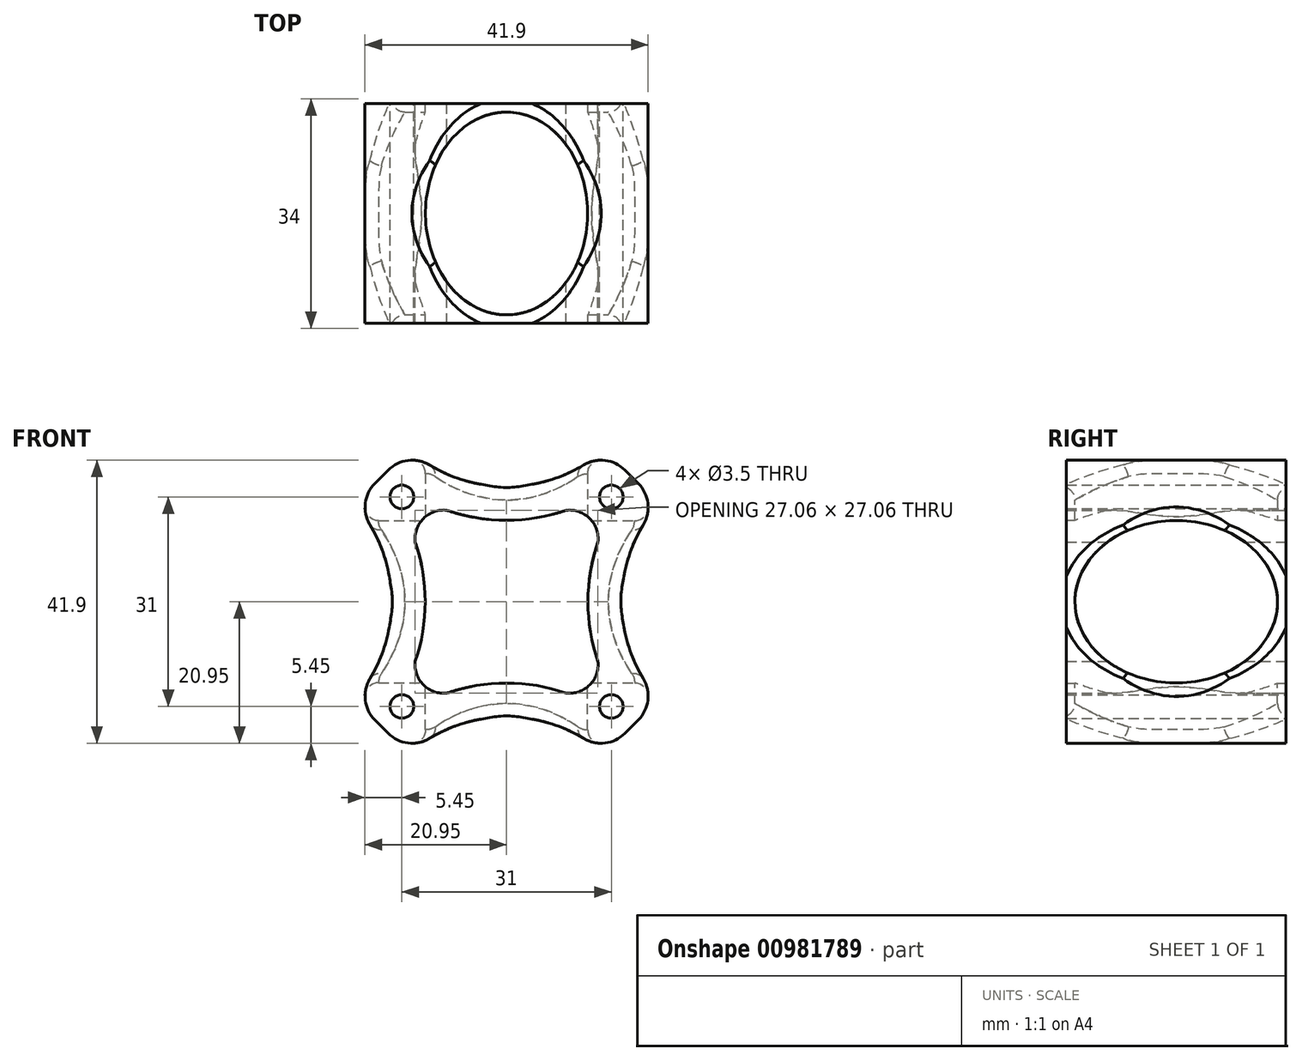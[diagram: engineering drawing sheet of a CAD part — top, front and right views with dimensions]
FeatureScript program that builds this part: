
annotation { "Feature Type Name" : "Feature", "Feature Type Description" : "" }
export const myFeature = defineFeature(function(context is Context, id is Id, definition is map)
    precondition{}
    {
        {
            var Q0;
            Q0=qCreatedBy(makeId("Front.planeOp"),FACE);
            var sketch = newSketch(context, id + "F0", { "sketchPlane" : qUnion([Q0])});
            skLineSegment(sketch, "E0.bottom", {"start": v(-15.5, 15.5) * mm, "end": v(15.5, 15.5) * mm, "construction": true});
            skLineSegment(sketch, "E0.top", {"start": v(-15.5, -15.5) * mm, "end": v(15.5, -15.5) * mm, "construction": true});
            skLineSegment(sketch, "E0.left", {"start": v(-15.5, 15.5) * mm, "end": v(-15.5, -15.5) * mm, "construction": true});
            skLineSegment(sketch, "E0.right", {"start": v(15.5, 15.5) * mm, "end": v(15.5, -15.5) * mm, "construction": true});
            skPoint(sketch, "E0.middle", {"position": v(0, 0) * mm});
            skCircle(sketch, "E1", {"center": v(-15.5, 15.5) * mm, "radius": 2.75 * mm, "construction": true});
            skCircle(sketch, "E2", {"center": v(15.5, 15.5) * mm, "radius": 2.75 * mm, "construction": true});
            skCircle(sketch, "E3", {"center": v(-15.5, -15.5) * mm, "radius": 2.75 * mm, "construction": true});
            skCircle(sketch, "E4", {"center": v(15.5, -15.5) * mm, "radius": 2.75 * mm, "construction": true});
            skCircle(sketch, "E5", {"center": v(0, 0) * mm, "radius": 6.6 * mm});
            skLineSegment(sketch, "E6.bottom", {"start": v(14.5, 22.5) * mm, "end": v(-14.5, 22.5) * mm});
            skLineSegment(sketch, "E6.top", {"start": v(14.5, -22.5) * mm, "end": v(-14.5, -22.5) * mm});
            skLineSegment(sketch, "E6.left", {"start": v(22.5, 14.5) * mm, "end": v(22.5, 0) * mm});
            skLineSegment(sketch, "E6.right", {"start": v(-22.5, 14.5) * mm, "end": v(-22.5, 0) * mm});
            skPoint(sketch, "E7.visualSharp", {"position": v(-22.5, 22.5) * mm});
            skPoint(sketch, "E8.visualSharp", {"position": v(22.5, 22.5) * mm});
            skPoint(sketch, "E9.visualSharp", {"position": v(22.5, -22.5) * mm});
            skPoint(sketch, "E10.visualSharp", {"position": v(-22.5, -22.5) * mm});
            skLineSegment(sketch, "E11", {"start": v(-22.5, 0) * mm, "end": v(-22.5, -14.5) * mm});
            skLineSegment(sketch, "E12", {"start": v(22.5, 0) * mm, "end": v(22.5, -14.5) * mm});
            skArc(sketch, "E13", {"start": v(-22.5, -14.5) * mm, "mid": v(-17.05, 0) * mm, "end": v(-22.5, 14.5) * mm});
            skArc(sketch, "E14", {"start": v(-14.5, 22.5) * mm, "mid": v(0, 17.05) * mm, "end": v(14.5, 22.5) * mm});
            skArc(sketch, "E15", {"start": v(22.5, 14.5) * mm, "mid": v(17.05, 0) * mm, "end": v(22.5, -14.5) * mm});
            skArc(sketch, "E16", {"start": v(14.5, -22.5) * mm, "mid": v(0, -17.05) * mm, "end": v(-14.5, -22.5) * mm});
            skArc(sketch, "E17", {"start": v(-8.83, 13.53) * mm, "mid": v(0, 12.05) * mm, "end": v(8.83, 13.53) * mm});
            skArc(sketch, "E18", {"start": v(-8.83, 13.53) * mm, "mid": v(-12.3, 12.3) * mm, "end": v(-13.53, 8.83) * mm});
            skArc(sketch, "E19.1.0", {"start": v(-13.53, -8.83) * mm, "mid": v(-12.3, -12.3) * mm, "end": v(-8.83, -13.53) * mm});
            skArc(sketch, "E19.2.0", {"start": v(8.83, -13.53) * mm, "mid": v(12.3, -12.3) * mm, "end": v(13.53, -8.83) * mm});
            skArc(sketch, "E19.3.0", {"start": v(13.53, 8.83) * mm, "mid": v(12.3, 12.3) * mm, "end": v(8.83, 13.53) * mm});
            skArc(sketch, "E20", {"start": v(13.53, 8.83) * mm, "mid": v(12.05, 0) * mm, "end": v(13.53, -8.83) * mm});
            skArc(sketch, "E21", {"start": v(8.83, -13.53) * mm, "mid": v(0, -12.05) * mm, "end": v(-8.83, -13.53) * mm});
            skArc(sketch, "E22", {"start": v(-13.53, -8.83) * mm, "mid": v(-12.05, 0) * mm, "end": v(-13.53, 8.83) * mm});
            skLineSegment(sketch, "E23", {"start": v(-22.5, 14.5) * mm, "end": v(-14.5, 22.5) * mm});
            skLineSegment(sketch, "E24", {"start": v(14.5, 22.5) * mm, "end": v(22.5, 14.5) * mm});
            skLineSegment(sketch, "E25", {"start": v(22.5, -14.5) * mm, "end": v(14.5, -22.5) * mm});
            skLineSegment(sketch, "E26", {"start": v(-14.5, -22.5) * mm, "end": v(-22.5, -14.5) * mm});
            skSolve(sketch);
        }
        {
            var Q0;
            Q0=makeQuery(id+"F0.imprint","IMPRINT",FACE,{"disambiguationData":[TD([[makeQuery(id+"F0.imprint","IMPRINT",EDGE,{"derivedFrom":sQuery(id+"F0.wireOp",EDGE,"E13")}),-1.0]])]});
            extrude(context, id + "F1", {"entities" : qUnion([Q0]), "depth" : 32.5 * mm, "offsetDistance" : 25 * mm});
        }
        {
            var Q0;
            Q0=sQuery(id+"F0.wireOp",VERTEX,"E0.bottom.end");
            var Q1;
            Q1=sQuery(id+"F0.wireOp",VERTEX,"E0.bottom.start");
            var Q2;
            Q2=sQuery(id+"F0.wireOp",VERTEX,"E0.top.start");
            var Q3;
            Q3=sQuery(id+"F0.wireOp",VERTEX,"E0.top.end");
            var Q4;
            Q4=makeQuery(id+"F1.opExtrude","SWEPT_BODY",BODY,{"disambiguationData":[OSD([sQuery(id+"F0.wireOp",EDGE,"E7.filletArc"),sQuery(id+"F0.wireOp",EDGE,"E8.filletArc"),sQuery(id+"F0.wireOp",EDGE,"E9.filletArc"),sQuery(id+"F0.wireOp",EDGE,"E10.filletArc"),sQuery(id+"F0.wireOp",EDGE,"E13"),sQuery(id+"F0.wireOp",EDGE,"E14"),sQuery(id+"F0.wireOp",EDGE,"E15"),sQuery(id+"F0.wireOp",EDGE,"E16"),sQuery(id+"F0.wireOp",EDGE,"E17"),sQuery(id+"F0.wireOp",EDGE,"E18"),sQuery(id+"F0.wireOp",EDGE,"E19.1.0"),sQuery(id+"F0.wireOp",EDGE,"E19.2.0"),sQuery(id+"F0.wireOp",EDGE,"E19.3.0"),sQuery(id+"F0.wireOp",EDGE,"E20"),sQuery(id+"F0.wireOp",EDGE,"E21"),sQuery(id+"F0.wireOp",EDGE,"E22")])]});
            hole(context, id + "F2", {"style" : HoleStyle.SIMPLE, "endStyle" : HoleEndStyle.THROUGH, "oppositeDirection" : true, "holeDiameter" : 3.5 * mm, "majorDiameter" : 5 * mm, "isTappedThrough" : true, "tappedDepth" : 12 * mm, "tapClearance" : 3, "locations" : qUnion([Q0, Q1, Q2, Q3]), "scope" : qUnion([Q4])});
        }
        {
            var Q0;
            Q0=makeQuery(id+"F1.opExtrude","SWEPT_EDGE",EDGE,{"disambiguationData":[OSD([sQuery(id+"F0.wireOp",EDGE,"E6.right"),sQuery(id+"F0.wireOp",EDGE,"E13"),sQuery(id+"F0.wireOp",EDGE,"E23")])]});
            var Q1;
            Q1=makeQuery(id+"F1.opExtrude","SWEPT_EDGE",EDGE,{"disambiguationData":[OSD([sQuery(id+"F0.wireOp",EDGE,"E6.bottom"),sQuery(id+"F0.wireOp",EDGE,"E14"),sQuery(id+"F0.wireOp",EDGE,"E23")])]});
            var Q2;
            Q2=makeQuery(id+"F1.opExtrude","SWEPT_EDGE",EDGE,{"disambiguationData":[OSD([sQuery(id+"F0.wireOp",EDGE,"E6.bottom"),sQuery(id+"F0.wireOp",EDGE,"E14"),sQuery(id+"F0.wireOp",EDGE,"E24")])]});
            var Q3;
            Q3=makeQuery(id+"F1.opExtrude","SWEPT_EDGE",EDGE,{"disambiguationData":[OSD([sQuery(id+"F0.wireOp",EDGE,"E6.left"),sQuery(id+"F0.wireOp",EDGE,"E15"),sQuery(id+"F0.wireOp",EDGE,"E24")])]});
            var Q4;
            Q4=makeQuery(id+"F1.opExtrude","SWEPT_EDGE",EDGE,{"disambiguationData":[OSD([sQuery(id+"F0.wireOp",EDGE,"E12"),sQuery(id+"F0.wireOp",EDGE,"E15"),sQuery(id+"F0.wireOp",EDGE,"E25")])]});
            var Q5;
            Q5=makeQuery(id+"F1.opExtrude","SWEPT_EDGE",EDGE,{"disambiguationData":[OSD([sQuery(id+"F0.wireOp",EDGE,"E6.top"),sQuery(id+"F0.wireOp",EDGE,"E16"),sQuery(id+"F0.wireOp",EDGE,"E25")])]});
            var Q6;
            Q6=makeQuery(id+"F1.opExtrude","SWEPT_EDGE",EDGE,{"disambiguationData":[OSD([sQuery(id+"F0.wireOp",EDGE,"E6.top"),sQuery(id+"F0.wireOp",EDGE,"E16"),sQuery(id+"F0.wireOp",EDGE,"E26")])]});
            var Q7;
            Q7=makeQuery(id+"F1.opExtrude","SWEPT_EDGE",EDGE,{"disambiguationData":[OSD([sQuery(id+"F0.wireOp",EDGE,"E11"),sQuery(id+"F0.wireOp",EDGE,"E13"),sQuery(id+"F0.wireOp",EDGE,"E26")])]});
            fillet(context, id + "F3", {"entities" : qUnion([Q0, Q1, Q2, Q3, Q4, Q5, Q6, Q7]), "radius" : 5 * mm, "tangentPropagation" : true, "allowEdgeOverflow" : false});
        }
        {
            var Q0;
            Q0=qCreatedBy(makeId("Right.planeOp"),FACE);
            cPlane(context, id + "F4", {"entities" : qUnion([Q0]), "cplaneType" : CPlaneType.OFFSET, "offset" : 25 * mm, "width" : 150 * mm, "height" : 150 * mm});
        }
        {
            var Q0;
            Q0=qCreatedBy(id+"F4.planeOp",FACE);
            var sketch = newSketch(context, id + "F5", { "sketchPlane" : qUnion([Q0])});
            skArc(sketch, "E27", {"start": v(-4.25, 0) * mm, "mid": v(-16.25, 12) * mm, "end": v(-28.25, 0) * mm, "construction": true});
            skLineSegment(sketch, "E28", {"start": v(0, 0) * mm, "end": v(-32.5, 0) * mm});
            skCircle(sketch, "E29", {"center": v(-16.25, 0) * mm, "radius": 12 * mm, "construction": true});
            skEllipse(sketch, "E30", {"center": v(-16.25, 0) * mm, "majorRadius": 12 * mm, "minorRadius": 15 * mm, "majorAxis": v(0, 1)});
            skSolve(sketch);
        }
        {
            var Q0;
            Q0=qSketchRegion(id+"F5",true);
            extrude(context, id + "F6", {"entities" : qUnion([Q0]), "operationType" : NewBodyOperationType.REMOVE, "oppositeDirection" : true, "depth" : 60 * mm, "offsetDistance" : 25 * mm});
        }
        {
            var Q0;
            Q0=qCreatedBy(makeId("Top.planeOp"),FACE);
            cPlane(context, id + "F7", {"entities" : qUnion([Q0]), "cplaneType" : CPlaneType.OFFSET, "offset" : 25 * mm, "width" : 150 * mm, "height" : 150 * mm});
        }
        {
            var Q0;
            Q0=qCreatedBy(id+"F7.planeOp",FACE);
            var sketch = newSketch(context, id + "F8", { "sketchPlane" : qUnion([Q0])});
            skLineSegment(sketch, "E31", {"start": v(0, 0) * mm, "end": v(0, -32.5) * mm});
            skCircle(sketch, "E32", {"center": v(0, -16.25) * mm, "radius": 12 * mm, "construction": true});
            skEllipse(sketch, "E33", {"center": v(0, -16.25) * mm, "majorRadius": 12 * mm, "minorRadius": 15 * mm, "majorAxis": v(-1, 0)});
            skSolve(sketch);
        }
        {
            var Q0;
            {var subQ0=sQuery(id+"F8.wireOp",EDGE,"E32");var subQ1=sQuery(id+"F8.wireOp",EDGE,"E31");var subQ2=makeQuery(id+"F8.imprint","INTERSECT",VERTEX,{"disambiguationData":[OD(0.0)],"derivedFrom":[subQ1,subQ0]});Q0=makeQuery(id+"F8.imprint","IMPRINT",FACE,{"disambiguationData":[TD([[makeQuery(id+"F8.imprint","IMPRINT",EDGE,{"disambiguationData":[TD([[subQ2,1.0]])],"derivedFrom":subQ1}),1.0]])]});}
            var Q1;
            {var subQ0=sQuery(id+"F8.wireOp",EDGE,"E32");var subQ1=sQuery(id+"F8.wireOp",EDGE,"E31");var subQ2=makeQuery(id+"F8.imprint","INTERSECT",VERTEX,{"disambiguationData":[OD(0.0)],"derivedFrom":[subQ1,subQ0]});Q1=makeQuery(id+"F8.imprint","IMPRINT",FACE,{"disambiguationData":[TD([[makeQuery(id+"F8.imprint","IMPRINT",EDGE,{"disambiguationData":[TD([[subQ2,1.0]])],"derivedFrom":subQ1}),-1.0]])]});}
            extrude(context, id + "F9", {"entities" : qUnion([Q0, Q1]), "operationType" : NewBodyOperationType.REMOVE, "oppositeDirection" : true, "depth" : 60 * mm, "offsetDistance" : 25 * mm});
        }
        {
            var Q0;
            Q0=makeQuery(id+"F9.boolean.opBoolean","INTERSECT",EDGE,{"disambiguationData":[OD(0.0)],"derivedFrom":[makeQuery(id+"F1.opExtrude","SWEPT_FACE",FACE,{"disambiguationData":[OSD([sQuery(id+"F0.wireOp",EDGE,"E14")])]}),makeQuery(id+"F9.opExtrude","SWEPT_FACE",FACE,{"disambiguationData":[OSD([sQuery(id+"F8.wireOp",EDGE,"E33")])]})]});
            var Q1;
            Q1=makeQuery(id+"F9.boolean.opBoolean","INTERSECT",EDGE,{"derivedFrom":[makeQuery(id+"F3.opFillet","BLEND_FACE",FACE,{"disambiguationData":[OSD([sQuery(id+"F0.wireOp",EDGE,"E6.bottom"),sQuery(id+"F0.wireOp",EDGE,"E14"),sQuery(id+"F0.wireOp",EDGE,"E23")])]}),makeQuery(id+"F9.opExtrude","SWEPT_FACE",FACE,{"disambiguationData":[OSD([sQuery(id+"F8.wireOp",EDGE,"E33")])]})]});
            var Q2;
            Q2=makeQuery(id+"F9.boolean.opBoolean","INTERSECT",EDGE,{"disambiguationData":[OD(1.0)],"derivedFrom":[makeQuery(id+"F1.opExtrude","SWEPT_FACE",FACE,{"disambiguationData":[OSD([sQuery(id+"F0.wireOp",EDGE,"E14")])]}),makeQuery(id+"F9.opExtrude","SWEPT_FACE",FACE,{"disambiguationData":[OSD([sQuery(id+"F8.wireOp",EDGE,"E33")])]})]});
            var Q3;
            Q3=makeQuery(id+"F9.boolean.opBoolean","INTERSECT",EDGE,{"derivedFrom":[makeQuery(id+"F3.opFillet","BLEND_FACE",FACE,{"disambiguationData":[OSD([sQuery(id+"F0.wireOp",EDGE,"E6.bottom"),sQuery(id+"F0.wireOp",EDGE,"E14"),sQuery(id+"F0.wireOp",EDGE,"E24")])]}),makeQuery(id+"F9.opExtrude","SWEPT_FACE",FACE,{"disambiguationData":[OSD([sQuery(id+"F8.wireOp",EDGE,"E33")])]})]});
            var Q4;
            Q4=makeQuery(id+"F6.boolean.opBoolean","INTERSECT",EDGE,{"disambiguationData":[OD(0.0)],"derivedFrom":[makeQuery(id+"F1.opExtrude","SWEPT_FACE",FACE,{"disambiguationData":[OSD([sQuery(id+"F0.wireOp",EDGE,"E13")])]}),makeQuery(id+"F6.opExtrude","SWEPT_FACE",FACE,{"disambiguationData":[OSD([sQuery(id+"F5.wireOp",EDGE,"E30")])]})]});
            var Q5;
            Q5=makeQuery(id+"F6.boolean.opBoolean","INTERSECT",EDGE,{"derivedFrom":[makeQuery(id+"F3.opFillet","BLEND_FACE",FACE,{"disambiguationData":[OSD([sQuery(id+"F0.wireOp",EDGE,"E6.left"),sQuery(id+"F0.wireOp",EDGE,"E15"),sQuery(id+"F0.wireOp",EDGE,"E24")])]}),makeQuery(id+"F6.opExtrude","SWEPT_FACE",FACE,{"disambiguationData":[OSD([sQuery(id+"F5.wireOp",EDGE,"E30")])]})]});
            var Q6;
            Q6=makeQuery(id+"F9.boolean.opBoolean","INTERSECT",EDGE,{"disambiguationData":[OD(0.0)],"derivedFrom":[makeQuery(id+"F1.opExtrude","SWEPT_FACE",FACE,{"disambiguationData":[OSD([sQuery(id+"F0.wireOp",EDGE,"E16")])]}),makeQuery(id+"F9.opExtrude","SWEPT_FACE",FACE,{"disambiguationData":[OSD([sQuery(id+"F8.wireOp",EDGE,"E33")])]})]});
            fillet(context, id + "F10", {"entities" : qUnion([Q0, Q1, Q2, Q3, Q4, Q5, Q6]), "radius" : 2 * mm, "tangentPropagation" : true, "allowEdgeOverflow" : false});
        }
    });
